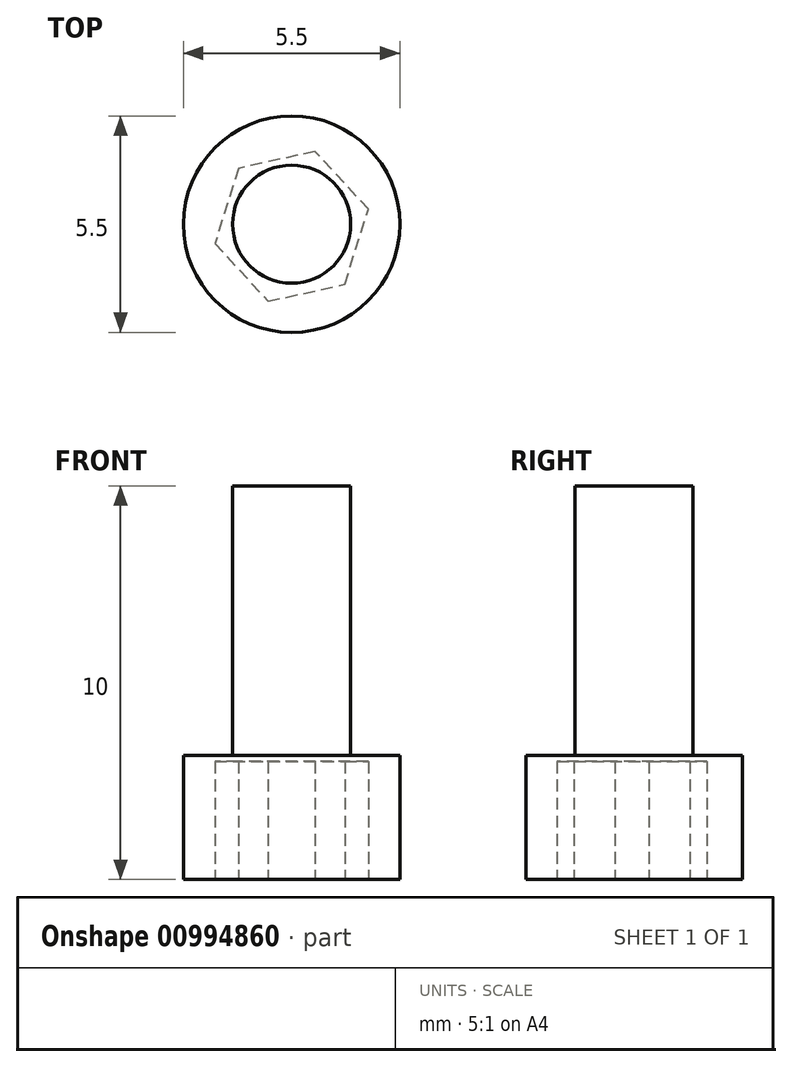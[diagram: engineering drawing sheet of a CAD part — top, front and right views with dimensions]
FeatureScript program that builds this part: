
annotation { "Feature Type Name" : "Feature", "Feature Type Description" : "" }
export const myFeature = defineFeature(function(context is Context, id is Id, definition is map)
    precondition{}
    {
        {
            var Q0;
            Q0=qCreatedBy(makeId("Top.planeOp"),FACE);
            var sketch = newSketch(context, id + "F0", { "sketchPlane" : qUnion([Q0])});
            skCircle(sketch, "E0", {"center": v(0, 0) * mm, "radius": 2.75 * mm});
            skCircle(sketch, "E1", {"center": v(0, 0) * mm, "radius": 1.5 * mm});
            skSolve(sketch);
        }
        {
            var Q0;
            Q0=makeQuery(id+"F0.imprint","IMPRINT",FACE,{"disambiguationData":[TD([[makeQuery(id+"F0.imprint","IMPRINT",EDGE,{"derivedFrom":sQuery(id+"F0.wireOp",EDGE,"E0")}),1.0]])]});
            extrude(context, id + "F1", {"entities" : qUnion([Q0]), "depth" : 3.15 * mm, "offsetDistance" : 25 * mm});
        }
        {
            var Q0;
            Q0=makeQuery(id+"F0.imprint","IMPRINT",FACE,{"disambiguationData":[TD([[makeQuery(id+"F0.imprint","IMPRINT",EDGE,{"derivedFrom":sQuery(id+"F0.wireOp",EDGE,"E1")}),1.0]])]});
            extrude(context, id + "F2", {"entities" : qUnion([Q0]), "operationType" : NewBodyOperationType.ADD, "depth" : 10 * mm, "offsetDistance" : 25 * mm});
        }
        {
            var Q0;
            {var subQ0=sQuery(id+"F0.wireOp",EDGE,"E1");Q0=makeQuery(id+"F2.boolean.opBoolean","MERGE",FACE,{"derivedFrom":[makeQuery(id+"F1.opExtrude","CAP_FACE",FACE,{"disambiguationData":[OSD([sQuery(id+"F0.wireOp",EDGE,"E0"),subQ0])],"isStart":true}),makeQuery(id+"F2.opExtrude","CAP_FACE",FACE,{"disambiguationData":[OSD([subQ0])],"isStart":true})]});}
            var sketch = newSketch(context, id + "F3", { "sketchPlane" : qUnion([Q0])});
            skCircle(sketch, "E2.cCircle", {"center": v(0, 0.05) * mm, "radius": 1.73 * mm, "construction": true});
            skLineSegment(sketch, "E2.0", {"start": v(-0.6, 1.96) * mm, "end": v(1.35, 1.52) * mm});
            skLineSegment(sketch, "E2.1", {"start": v(1.35, 1.52) * mm, "end": v(1.95, -0.38) * mm});
            skLineSegment(sketch, "E2.2", {"start": v(1.95, -0.38) * mm, "end": v(0.6, -1.85) * mm});
            skLineSegment(sketch, "E2.3", {"start": v(0.6, -1.85) * mm, "end": v(-1.35, -1.42) * mm});
            skLineSegment(sketch, "E2.4", {"start": v(-1.35, -1.42) * mm, "end": v(-1.95, 0.49) * mm});
            skLineSegment(sketch, "E2.5", {"start": v(-1.95, 0.49) * mm, "end": v(-0.6, 1.96) * mm});
            skPoint(sketch, "E2.0.midPoint", {"position": v(0.38, 1.74) * mm});
            skSolve(sketch);
        }
        {
            var Q0;
            Q0 = qSketchRegion(id + "F3", true);
            extrude(context, id + "F4", {"entities" : qUnion([Q0]), "operationType" : NewBodyOperationType.REMOVE, "oppositeDirection" : true, "depth" : 3 * mm, "offsetDistance" : 25 * mm});
        }
    });
